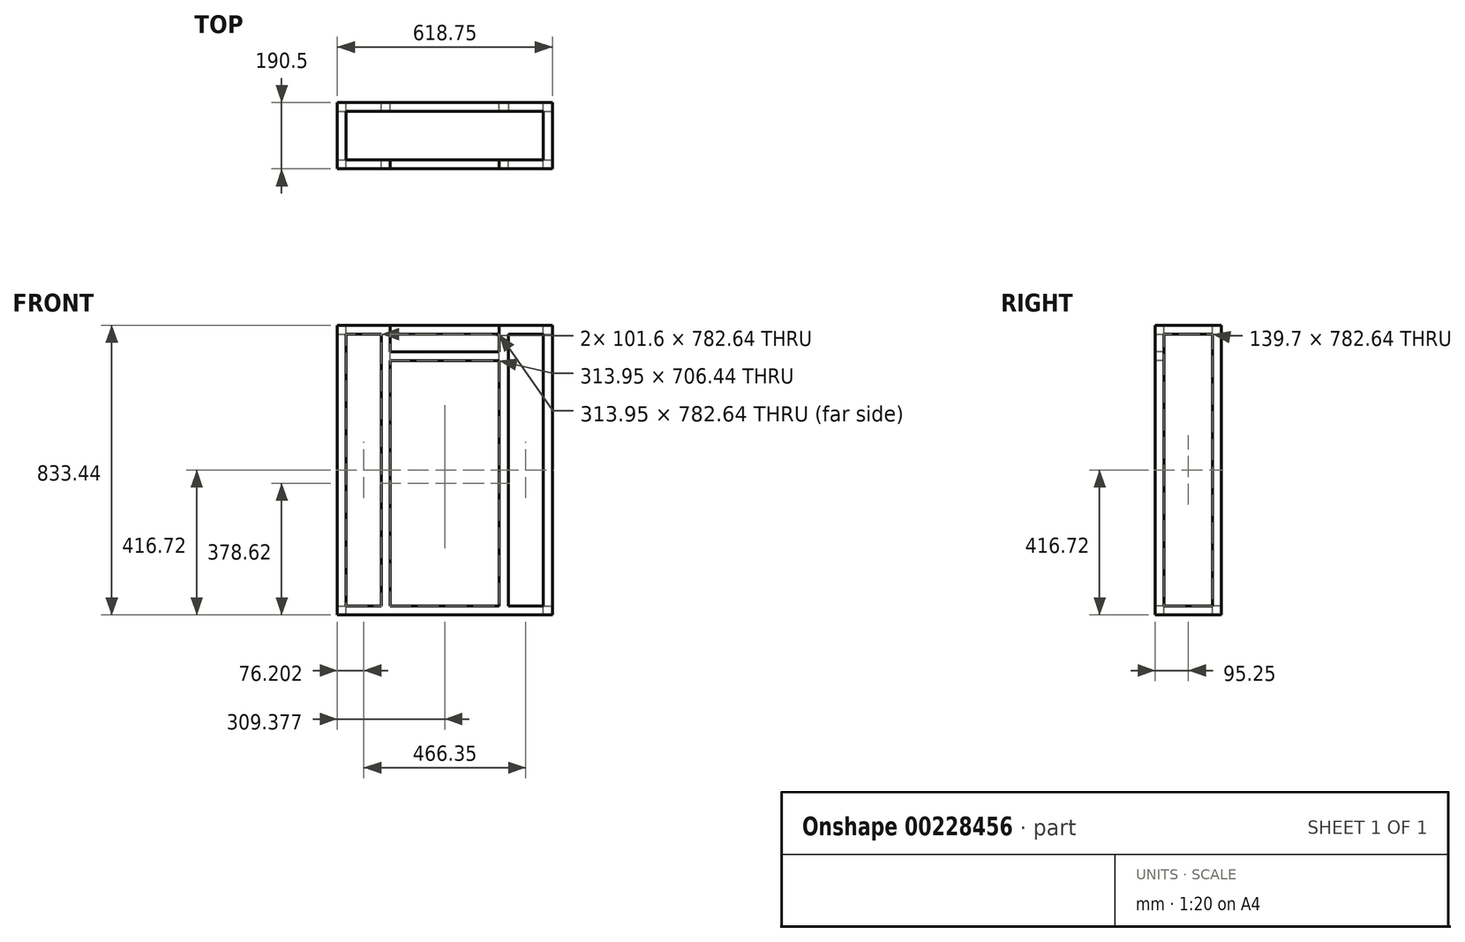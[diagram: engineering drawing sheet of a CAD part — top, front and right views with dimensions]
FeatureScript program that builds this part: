
annotation { "Feature Type Name" : "Feature", "Feature Type Description" : "" }
export const myFeature = defineFeature(function(context is Context, id is Id, definition is map)
    precondition{}
    {
        {
            var Q0;
            Q0=qCreatedBy(makeId("Front.planeOp"),FACE);
            var sketch = newSketch(context, id + "F0", { "sketchPlane" : qUnion([Q0])});
            skLineSegment(sketch, "E0.bottom", {"start": v(-329.36, 695.98) * mm, "end": v(289.4, 695.98) * mm});
            skLineSegment(sketch, "E0.top", {"start": v(-329.36, -137.46) * mm, "end": v(289.4, -137.46) * mm});
            skLineSegment(sketch, "E0.left", {"start": v(-329.36, 695.98) * mm, "end": v(-329.36, -137.46) * mm});
            skLineSegment(sketch, "E0.right", {"start": v(289.4, 695.98) * mm, "end": v(289.4, -137.46) * mm});
            skSolve(sketch);
        }
        {
            var Q0;
            Q0=makeQuery(id+"F0.imprint","IMPRINT",FACE,{"disambiguationData":[TD([[makeQuery(id+"F0.imprint","IMPRINT",EDGE,{"derivedFrom":sQuery(id+"F0.wireOp",EDGE,"E0.bottom")}),-1.0]])]});
            extrude(context, id + "F1", {"entities" : qUnion([Q0]), "depth" : 190.5 * mm});
        }
        {
            var Q0;
            Q0=makeQuery(id+"F1.opExtrude","SWEPT_FACE",FACE,{"disambiguationData":[OSD([sQuery(id+"F0.wireOp",EDGE,"E0.bottom")])]});
            var sketch = newSketch(context, id + "F2", { "sketchPlane" : qUnion([Q0])});
            skLineSegment(sketch, "E1.bottom", {"start": v(-329.36, -190.5) * mm, "end": v(289.4, -190.5) * mm});
            skLineSegment(sketch, "E1.top", {"start": v(-329.36, 0) * mm, "end": v(289.4, 0) * mm});
            skLineSegment(sketch, "E1.left", {"start": v(-329.36, -190.5) * mm, "end": v(-329.36, 0) * mm});
            skLineSegment(sketch, "E1.right", {"start": v(289.4, -190.5) * mm, "end": v(289.4, 0) * mm});
            skLineSegment(sketch, "E2.0", {"start": v(264, -25.4) * mm, "end": v(-303.96, -25.4) * mm});
            skLineSegment(sketch, "E2.1", {"start": v(264, -165.1) * mm, "end": v(264, -25.4) * mm});
            skLineSegment(sketch, "E2.2", {"start": v(-303.96, -165.1) * mm, "end": v(264, -165.1) * mm});
            skLineSegment(sketch, "E2.3", {"start": v(-303.96, -25.4) * mm, "end": v(-303.96, -165.1) * mm});
            skSolve(sketch);
        }
        {
            var Q0;
            Q0=makeQuery(id+"F2.imprint","IMPRINT",FACE,{"disambiguationData":[TD([[makeQuery(id+"F2.imprint","IMPRINT",EDGE,{"derivedFrom":sQuery(id+"F2.wireOp",EDGE,"E2.0")}),1.0]])]});
            extrude(context, id + "F3", {"entities" : qUnion([Q0]), "operationType" : NewBodyOperationType.REMOVE, "endBound" : BoundingType.THROUGH_ALL, "oppositeDirection" : true, "depth" : 25 * mm});
        }
        {
            var Q0;
            Q0=makeQuery(id+"F1.opExtrude","CAP_FACE",FACE,{"disambiguationData":[OSD([sQuery(id+"F0.wireOp",EDGE,"E0.bottom"),sQuery(id+"F0.wireOp",EDGE,"E0.top"),sQuery(id+"F0.wireOp",EDGE,"E0.left"),sQuery(id+"F0.wireOp",EDGE,"E0.right")])],"isStart":true});
            var sketch = newSketch(context, id + "F4", { "sketchPlane" : qUnion([Q0])});
            skLineSegment(sketch, "E3.bottom", {"start": v(-289.4, 695.98) * mm, "end": v(329.36, 695.98) * mm});
            skLineSegment(sketch, "E3.top", {"start": v(-289.4, -137.46) * mm, "end": v(329.36, -137.46) * mm});
            skLineSegment(sketch, "E3.left", {"start": v(-289.4, 695.98) * mm, "end": v(-289.4, -137.46) * mm});
            skLineSegment(sketch, "E3.right", {"start": v(329.36, 695.98) * mm, "end": v(329.36, -137.46) * mm});
            skLineSegment(sketch, "E4.0", {"start": v(303.96, -112.06) * mm, "end": v(303.96, 670.58) * mm});
            skLineSegment(sketch, "E4.1", {"start": v(-264, -112.06) * mm, "end": v(303.96, -112.06) * mm});
            skLineSegment(sketch, "E4.2", {"start": v(-264, 670.58) * mm, "end": v(-264, -112.06) * mm});
            skLineSegment(sketch, "E4.3", {"start": v(303.96, 670.58) * mm, "end": v(-264, 670.58) * mm});
            skSolve(sketch);
        }
        {
            var Q0;
            Q0=makeQuery(id+"F4.imprint","IMPRINT",FACE,{"disambiguationData":[TD([[makeQuery(id+"F4.imprint","IMPRINT",EDGE,{"derivedFrom":sQuery(id+"F4.wireOp",EDGE,"E4.0")}),1.0]])]});
            extrude(context, id + "F5", {"entities" : qUnion([Q0]), "operationType" : NewBodyOperationType.REMOVE, "endBound" : BoundingType.THROUGH_ALL, "oppositeDirection" : true, "depth" : 25 * mm});
        }
        {
            var Q0;
            Q0=makeQuery(id+"F1.opExtrude","SWEPT_FACE",FACE,{"disambiguationData":[OSD([sQuery(id+"F0.wireOp",EDGE,"E0.right")])]});
            var sketch = newSketch(context, id + "F6", { "sketchPlane" : qUnion([Q0])});
            skLineSegment(sketch, "E5.0", {"start": v(-25.4, -112.06) * mm, "end": v(-25.4, 670.58) * mm});
            skLineSegment(sketch, "E5.1", {"start": v(-165.1, -112.06) * mm, "end": v(-25.4, -112.06) * mm});
            skLineSegment(sketch, "E5.2", {"start": v(-165.1, 670.58) * mm, "end": v(-165.1, -112.06) * mm});
            skLineSegment(sketch, "E5.3", {"start": v(-25.4, 670.58) * mm, "end": v(-165.1, 670.58) * mm});
            skSolve(sketch);
        }
        {
            var Q0;
            Q0=makeQuery(id+"F6.imprint","IMPRINT",FACE,{"disambiguationData":[TD([[makeQuery(id+"F6.imprint","IMPRINT",EDGE,{"derivedFrom":sQuery(id+"F6.wireOp",EDGE,"E5.0")}),1.0]])]});
            extrude(context, id + "F7", {"entities" : qUnion([Q0]), "operationType" : NewBodyOperationType.REMOVE, "endBound" : BoundingType.THROUGH_ALL, "oppositeDirection" : true, "depth" : 25 * mm});
        }
        {
            var Q0;
            Q0=makeQuery(id+"F5.boolean.opBoolean","COPY",FACE,{"disambiguationData":[TD([makeQuery(id+"F3.boolean.opBoolean","COPY",FACE,{"derivedFrom":makeQuery(id+"F3.opExtrude","SWEPT_FACE",FACE,{"disambiguationData":[OSD([sQuery(id+"F2.wireOp",EDGE,"E2.2")])]})})])],"derivedFrom":makeQuery(id+"F5.opExtrude","SWEPT_FACE",FACE,{"disambiguationData":[OSD([sQuery(id+"F4.wireOp",EDGE,"E4.3")])]})});
            var sketch = newSketch(context, id + "F8", { "sketchPlane" : qUnion([Q0])});
            skLineSegment(sketch, "E6.bottom", {"start": v(264, 190.5) * mm, "end": v(162.4, 190.5) * mm});
            skLineSegment(sketch, "E6.top", {"start": v(264, 165.1) * mm, "end": v(162.4, 165.1) * mm});
            skLineSegment(sketch, "E6.left", {"start": v(264, 190.5) * mm, "end": v(264, 165.1) * mm});
            skLineSegment(sketch, "E6.right", {"start": v(162.4, 190.5) * mm, "end": v(162.4, 165.1) * mm});
            skLineSegment(sketch, "E7.bottom", {"start": v(162.4, 165.1) * mm, "end": v(137, 165.1) * mm});
            skLineSegment(sketch, "E7.top", {"start": v(162.4, 190.5) * mm, "end": v(137, 190.5) * mm});
            skLineSegment(sketch, "E7.left", {"start": v(162.4, 165.1) * mm, "end": v(162.4, 190.5) * mm});
            skLineSegment(sketch, "E7.right", {"start": v(137, 165.1) * mm, "end": v(137, 190.5) * mm});
            skSolve(sketch);
        }
        {
            var Q0;
            Q0=makeQuery(id+"F8.imprint","IMPRINT",FACE,{"disambiguationData":[TD([[makeQuery(id+"F8.imprint","IMPRINT",EDGE,{"derivedFrom":sQuery(id+"F8.wireOp",EDGE,"E7.bottom")}),-1.0]])]});
            extrude(context, id + "F9", {"entities" : qUnion([Q0]), "operationType" : NewBodyOperationType.ADD, "depth" : 787.4 * mm});
        }
        {
            var Q0;
            {var subQ1=makeQuery(id+"F3.boolean.opBoolean","COPY",FACE,{"derivedFrom":makeQuery(id+"F3.opExtrude","SWEPT_FACE",FACE,{"disambiguationData":[OSD([sQuery(id+"F2.wireOp",EDGE,"E2.3")])]})});var subQ2=makeQuery(id+"F3.boolean.opBoolean","COPY",FACE,{"derivedFrom":makeQuery(id+"F3.opExtrude","SWEPT_FACE",FACE,{"disambiguationData":[OSD([sQuery(id+"F2.wireOp",EDGE,"E2.2")])]})});var subQ10=makeQuery(id+"F5.opExtrude","SWEPT_FACE",FACE,{"disambiguationData":[OSD([sQuery(id+"F4.wireOp",EDGE,"E4.3")])]});var subQ11=makeQuery(id+"F5.boolean.opBoolean","COPY",FACE,{"disambiguationData":[TD([subQ2])],"derivedFrom":subQ10});Q0=makeQuery(id+"F9.boolean.opBoolean","SPLIT",FACE,{"disambiguationData":[TD([subQ1])],"derivedFrom":subQ11});}
            var sketch = newSketch(context, id + "F10", { "sketchPlane" : qUnion([Q0])});
            skLineSegment(sketch, "E8", {"start": v(-303.96, 190.5) * mm, "end": v(-202.36, 190.5) * mm});
            skLineSegment(sketch, "E9.bottom", {"start": v(-202.36, 190.5) * mm, "end": v(-176.96, 190.5) * mm});
            skLineSegment(sketch, "E9.top", {"start": v(-202.36, 165.1) * mm, "end": v(-176.96, 165.1) * mm});
            skLineSegment(sketch, "E9.left", {"start": v(-202.36, 190.5) * mm, "end": v(-202.36, 165.1) * mm});
            skLineSegment(sketch, "E9.right", {"start": v(-176.96, 190.5) * mm, "end": v(-176.96, 165.1) * mm});
            skSolve(sketch);
        }
        {
            var Q0;
            Q0 = qSketchRegion(id + "F10", true);
            extrude(context, id + "F11", {"entities" : qUnion([Q0]), "operationType" : NewBodyOperationType.ADD, "depth" : 787.4 * mm});
        }
        {
            var Q0;
            Q0=makeQuery(id+"F5.boolean.opBoolean","COPY",FACE,{"disambiguationData":[TD([makeQuery(id+"F3.boolean.opBoolean","COPY",FACE,{"derivedFrom":makeQuery(id+"F3.opExtrude","SWEPT_FACE",FACE,{"disambiguationData":[OSD([sQuery(id+"F2.wireOp",EDGE,"E2.0")])]})})])],"derivedFrom":makeQuery(id+"F5.opExtrude","SWEPT_FACE",FACE,{"disambiguationData":[OSD([sQuery(id+"F4.wireOp",EDGE,"E4.3")])]})});
            var sketch = newSketch(context, id + "F12", { "sketchPlane" : qUnion([Q0])});
            skLineSegment(sketch, "E10", {"start": v(-303.96, 25.4) * mm, "end": v(-202.36, 25.4) * mm});
            skLineSegment(sketch, "E11.bottom", {"start": v(-202.36, 25.4) * mm, "end": v(-176.96, 25.4) * mm});
            skLineSegment(sketch, "E11.top", {"start": v(-202.36, 0) * mm, "end": v(-176.96, 0) * mm});
            skLineSegment(sketch, "E11.left", {"start": v(-202.36, 25.4) * mm, "end": v(-202.36, 0) * mm});
            skLineSegment(sketch, "E11.right", {"start": v(-176.96, 25.4) * mm, "end": v(-176.96, 0) * mm});
            skSolve(sketch);
        }
        {
            var Q0;
            Q0 = qSketchRegion(id + "F12", true);
            extrude(context, id + "F13", {"entities" : qUnion([Q0]), "operationType" : NewBodyOperationType.ADD, "depth" : 787.4 * mm});
        }
        {
            var Q0;
            {var subQ1=makeQuery(id+"F3.boolean.opBoolean","COPY",FACE,{"derivedFrom":makeQuery(id+"F3.opExtrude","SWEPT_FACE",FACE,{"disambiguationData":[OSD([sQuery(id+"F2.wireOp",EDGE,"E2.0")])]})});var subQ2=makeQuery(id+"F3.boolean.opBoolean","COPY",FACE,{"derivedFrom":makeQuery(id+"F3.opExtrude","SWEPT_FACE",FACE,{"disambiguationData":[OSD([sQuery(id+"F2.wireOp",EDGE,"E2.1")])]})});var subQ11=makeQuery(id+"F5.opExtrude","SWEPT_FACE",FACE,{"disambiguationData":[OSD([sQuery(id+"F4.wireOp",EDGE,"E4.3")])]});var subQ12=makeQuery(id+"F5.boolean.opBoolean","COPY",FACE,{"disambiguationData":[TD([subQ1])],"derivedFrom":subQ11});Q0=makeQuery(id+"F13.boolean.opBoolean","SPLIT",FACE,{"disambiguationData":[TD([subQ2])],"derivedFrom":subQ12});}
            var sketch = newSketch(context, id + "F14", { "sketchPlane" : qUnion([Q0])});
            skLineSegment(sketch, "E12", {"start": v(264, 25.4) * mm, "end": v(162.4, 25.4) * mm});
            skLineSegment(sketch, "E13.bottom", {"start": v(162.4, 25.4) * mm, "end": v(137, 25.4) * mm});
            skLineSegment(sketch, "E13.top", {"start": v(162.4, 0) * mm, "end": v(137, 0) * mm});
            skLineSegment(sketch, "E13.left", {"start": v(162.4, 25.4) * mm, "end": v(162.4, 0) * mm});
            skLineSegment(sketch, "E13.right", {"start": v(137, 25.4) * mm, "end": v(137, 0) * mm});
            skSolve(sketch);
        }
        {
            var Q0;
            Q0=makeQuery(id+"F14.imprint","IMPRINT",FACE,{"disambiguationData":[TD([[makeQuery(id+"F14.imprint","IMPRINT",EDGE,{"derivedFrom":sQuery(id+"F14.wireOp",EDGE,"E13.bottom")}),-1.0]])]});
            extrude(context, id + "F15", {"entities" : qUnion([Q0]), "operationType" : NewBodyOperationType.ADD, "depth" : 787.4 * mm});
        }
        {
            var Q0;
            Q0=makeQuery(id+"F11.opExtrude","SWEPT_FACE",FACE,{"disambiguationData":[OSD([sQuery(id+"F10.wireOp",EDGE,"E9.right")])]});
            var sketch = newSketch(context, id + "F16", { "sketchPlane" : qUnion([Q0])});
            skLineSegment(sketch, "E14", {"start": v(-190.5, 670.58) * mm, "end": v(-190.5, 619.78) * mm});
            skLineSegment(sketch, "E15.bottom", {"start": v(-190.5, 619.78) * mm, "end": v(-165.1, 619.78) * mm});
            skLineSegment(sketch, "E15.top", {"start": v(-190.5, 594.38) * mm, "end": v(-165.1, 594.38) * mm});
            skLineSegment(sketch, "E15.left", {"start": v(-190.5, 619.78) * mm, "end": v(-190.5, 594.38) * mm});
            skLineSegment(sketch, "E15.right", {"start": v(-165.1, 619.78) * mm, "end": v(-165.1, 594.38) * mm});
            skSolve(sketch);
        }
        {
            var Q0;
            Q0 = qSketchRegion(id + "F16", true);
            var Q1;
            Q1=makeQuery(id+"F9.opExtrude","SWEPT_FACE",FACE,{"disambiguationData":[OSD([sQuery(id+"F8.wireOp",EDGE,"E7.right")])]});
            extrude(context, id + "F17", {"entities" : qUnion([Q0]), "operationType" : NewBodyOperationType.ADD, "endBound" : BoundingType.UP_TO_SURFACE, "endBoundEntityFace" : qUnion([Q1]), "depth" : 381 * mm});
        }
        {
            var Q0;
            Q0=makeQuery(id+"F17.boolean.opBoolean","MERGE",FACE,{"derivedFrom":[makeQuery(id+"F11.boolean.opBoolean","MERGE",FACE,{"derivedFrom":[makeQuery(id+"F9.boolean.opBoolean","MERGE",FACE,{"derivedFrom":[makeQuery(id+"F1.opExtrude","CAP_FACE",FACE,{"disambiguationData":[OSD([sQuery(id+"F0.wireOp",EDGE,"E0.bottom"),sQuery(id+"F0.wireOp",EDGE,"E0.top"),sQuery(id+"F0.wireOp",EDGE,"E0.left"),sQuery(id+"F0.wireOp",EDGE,"E0.right")])],"isStart":false}),makeQuery(id+"F9.opExtrude","SWEPT_FACE",FACE,{"disambiguationData":[OSD([sQuery(id+"F8.wireOp",EDGE,"E7.top")])]})]}),makeQuery(id+"F11.opExtrude","SWEPT_FACE",FACE,{"disambiguationData":[OSD([sQuery(id+"F10.wireOp",EDGE,"E9.bottom")])]})]}),makeQuery(id+"F17.opExtrude","SWEPT_FACE",FACE,{"disambiguationData":[OSD([sQuery(id+"F16.wireOp",EDGE,"E15.left")])]})]});
            var sketch = newSketch(context, id + "F18", { "sketchPlane" : qUnion([Q0])});
            skLineSegment(sketch, "E16.bottom", {"start": v(-176.96, 670.58) * mm, "end": v(137, 670.58) * mm});
            skLineSegment(sketch, "E16.top", {"start": v(-176.96, 695.98) * mm, "end": v(137, 695.98) * mm});
            skLineSegment(sketch, "E16.left", {"start": v(-176.96, 670.58) * mm, "end": v(-176.96, 695.98) * mm});
            skLineSegment(sketch, "E16.right", {"start": v(137, 670.58) * mm, "end": v(137, 695.98) * mm});
            skSolve(sketch);
        }
        {
            var Q0;
            Q0=makeQuery(id+"F18.imprint","IMPRINT",FACE,{"disambiguationData":[TD([[makeQuery(id+"F18.imprint","IMPRINT",EDGE,{"derivedFrom":sQuery(id+"F18.wireOp",EDGE,"E16.bottom")}),-1.0]])]});
            extrude(context, id + "F19", {"entities" : qUnion([Q0]), "operationType" : NewBodyOperationType.REMOVE, "endBound" : BoundingType.UP_TO_NEXT, "oppositeDirection" : true, "depth" : 25 * mm});
        }
    });
